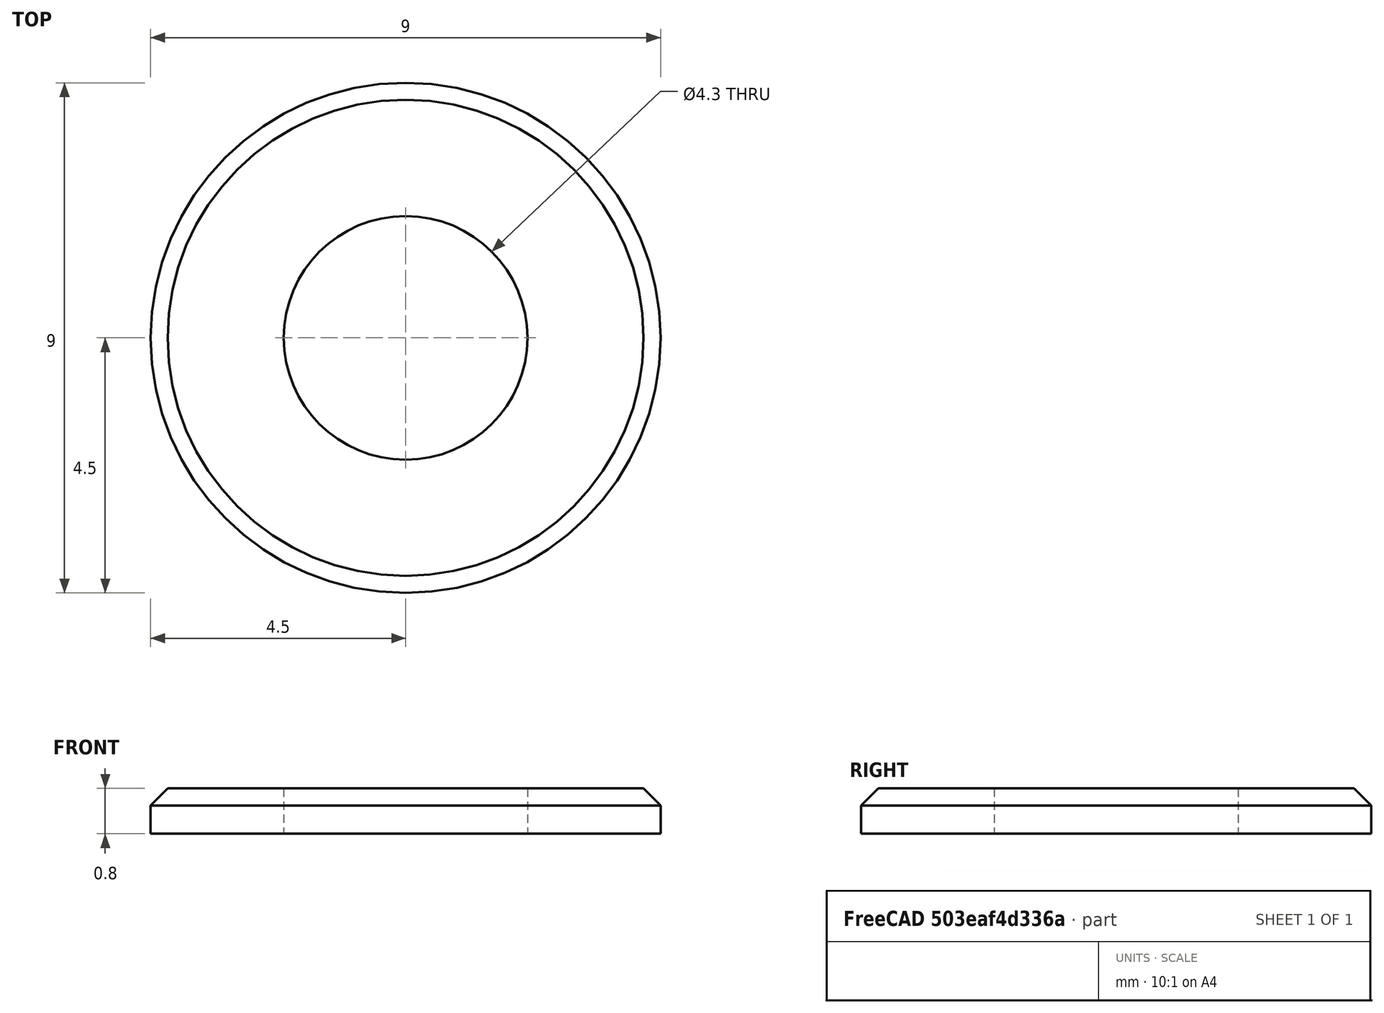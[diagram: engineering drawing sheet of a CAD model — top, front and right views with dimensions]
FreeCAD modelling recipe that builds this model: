
FCSTD DOCUMENT  (FreeCAD 0.15R4651 (Git))
Label: Scheibe_DIN125-B 4,3
License: CC-BY 3.0
LicenseURL: http://creativecommons.org/licenses/by/3.0/
objects: Sketcher::SketchObject×1, PartDesign::Revolution×1
note: 3 computed .brp shape members not serialized (recipe doc carries the construction recipe); baked Part::Feature solids carry a one-line shape summary decoded from their .brp

FEATURE [Sketcher::SketchObject] Sketch
  Placement = pos=(0,0,0) rot=(0.57735,0.57735,0.57735;2.0944rad)
  sketch-geometry (5):
    g0: LineSegment StartX=2.15 StartY=0 StartZ=0 EndX=4.5 EndY=0 EndZ=0
    g1: LineSegment StartX=4.5 StartY=0 StartZ=0 EndX=4.5 EndY=0.5 EndZ=0
    g2: LineSegment StartX=4.2 StartY=0.8 StartZ=0 EndX=2.15 EndY=0.8 EndZ=0
    g3: LineSegment StartX=2.15 StartY=0.8 StartZ=0 EndX=2.15 EndY=0 EndZ=0
    g4: LineSegment StartX=4.2 StartY=0.8 StartZ=0 EndX=4.5 EndY=0.5 EndZ=0
  constraints (15):
    c: Coincident(g0,g1)
    c: Coincident(g2,g3)
    c: Coincident(g3,g0)
    c: Horizontal(g0)
    c: Horizontal(g2)
    c: Vertical(g1)
    c: Vertical(g3)
    c: PointOnObject(g0,g-1)
    c: DistanceX(g-1,g2) = 2.15
    c: Coincident(g4,g2)
    c: Coincident(g4,g1)
    c: DistanceY(g3) = -0.8
    c: DistanceX(g-1,g1) = 4.5
    c: DistanceY(g4) = -0.3
    c: DistanceX(g4) = 0.3
FEATURE [PartDesign::Revolution] Revolution  label="Scheibe DIN 125 - B 4,3 #"
  Angle = 360
  Axis = (0,0,1)
  Base = (0,0,0)
  Placement = pos=(0,0,0) rot=(0.57735,0.57735,0.57735;2.0944rad)
  ReferenceAxis = -> Sketch [V_Axis]
  Reversed = true
  Sketch = -> Sketch
